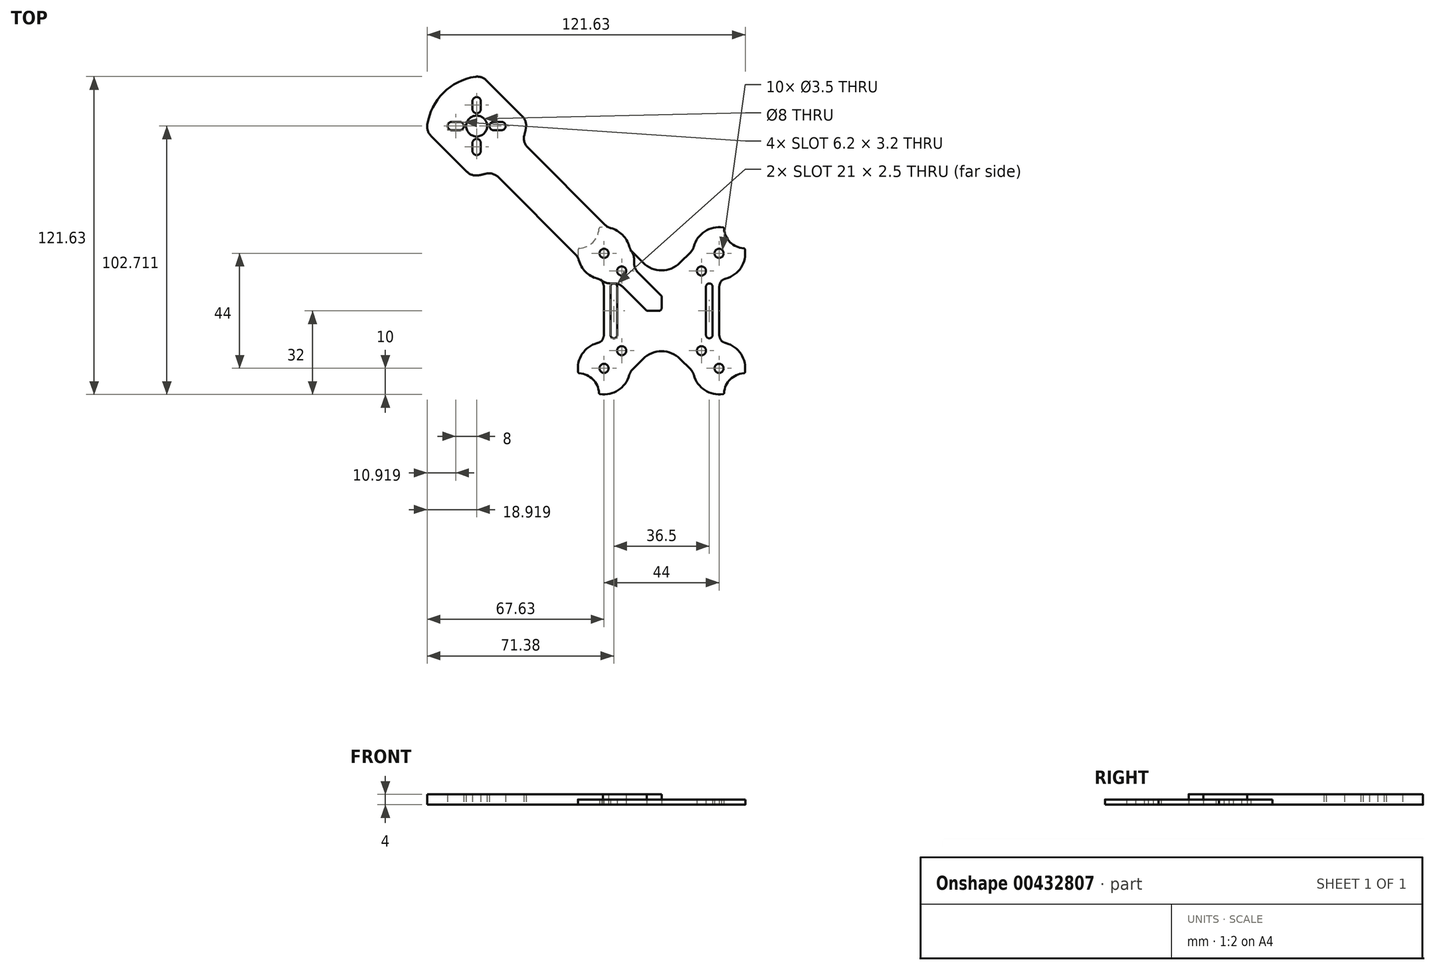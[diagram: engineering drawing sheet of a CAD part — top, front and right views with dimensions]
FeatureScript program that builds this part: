
annotation { "Feature Type Name" : "Feature", "Feature Type Description" : "" }
export const myFeature = defineFeature(function(context is Context, id is Id, definition is map)
    precondition{}
    {
        {
            var Q0;
            Q0=qCreatedBy(makeId("Top.planeOp"),FACE);
            var sketch = newSketch(context, id + "F0", { "sketchPlane" : qUnion([Q0])});
            skCircle(sketch, "E0", {"center": v(0, 0) * mm, "radius": 100 * mm, "construction": true});
            skLineSegment(sketch, "E1", {"start": v(0, 0) * mm, "end": v(-70.71, 70.71) * mm, "construction": true});
            skLineSegment(sketch, "E2", {"start": v(-53.4, 64.72) * mm, "end": v(-21.63, 32.95) * mm});
            skLineSegment(sketch, "E3", {"start": v(-64.72, 53.4) * mm, "end": v(-32.95, 21.63) * mm});
            skCircle(sketch, "E4", {"center": v(-70.71, 70.71) * mm, "radius": 4 * mm});
            skLineSegment(sketch, "E5", {"start": v(-70.71, 70.71) * mm, "end": v(-86.27, 86.27) * mm, "construction": true});
            skLineSegment(sketch, "E6", {"start": v(-70.71, 70.71) * mm, "end": v(-70.71, 77.21) * mm, "construction": true});
            skLineSegment(sketch, "E7", {"start": v(-70.71, 77.21) * mm, "end": v(-70.71, 80.21) * mm, "construction": true});
            skArc(sketch, "E8.0.startCap", {"start": v(-69.11, 77.21) * mm, "mid": v(-70.71, 75.61) * mm, "end": v(-72.31, 77.21) * mm});
            skArc(sketch, "E8.0.endCap", {"start": v(-72.31, 80.21) * mm, "mid": v(-70.71, 81.81) * mm, "end": v(-69.11, 80.21) * mm});
            skLineSegment(sketch, "E8.0.left", {"start": v(-72.31, 77.21) * mm, "end": v(-72.31, 80.21) * mm});
            skLineSegment(sketch, "E8.0.right", {"start": v(-69.11, 77.21) * mm, "end": v(-69.11, 80.21) * mm});
            skArc(sketch, "E9.1.0", {"start": v(-80.21, 69.11) * mm, "mid": v(-81.81, 70.71) * mm, "end": v(-80.21, 72.31) * mm});
            skLineSegment(sketch, "E9.1.1", {"start": v(-77.21, 69.11) * mm, "end": v(-80.21, 69.11) * mm});
            skArc(sketch, "E9.1.2", {"start": v(-77.21, 72.31) * mm, "mid": v(-75.61, 70.71) * mm, "end": v(-77.21, 69.11) * mm});
            skLineSegment(sketch, "E9.1.3", {"start": v(-77.21, 72.31) * mm, "end": v(-80.21, 72.31) * mm});
            skLineSegment(sketch, "E9.1.4", {"start": v(-77.21, 70.71) * mm, "end": v(-80.21, 70.71) * mm, "construction": true});
            skLineSegment(sketch, "E9.1.5", {"start": v(-70.71, 70.71) * mm, "end": v(-77.21, 70.71) * mm, "construction": true});
            skArc(sketch, "E9.2.0", {"start": v(-69.11, 61.21) * mm, "mid": v(-70.71, 59.61) * mm, "end": v(-72.31, 61.21) * mm});
            skLineSegment(sketch, "E9.2.1", {"start": v(-69.11, 64.21) * mm, "end": v(-69.11, 61.21) * mm});
            skArc(sketch, "E9.2.2", {"start": v(-72.31, 64.21) * mm, "mid": v(-70.71, 65.81) * mm, "end": v(-69.11, 64.21) * mm});
            skLineSegment(sketch, "E9.2.3", {"start": v(-72.31, 64.21) * mm, "end": v(-72.31, 61.21) * mm});
            skLineSegment(sketch, "E9.2.4", {"start": v(-70.71, 64.21) * mm, "end": v(-70.71, 61.21) * mm, "construction": true});
            skLineSegment(sketch, "E9.2.5", {"start": v(-70.71, 70.71) * mm, "end": v(-70.71, 64.21) * mm, "construction": true});
            skArc(sketch, "E9.3.0", {"start": v(-61.21, 72.31) * mm, "mid": v(-59.61, 70.71) * mm, "end": v(-61.21, 69.11) * mm});
            skLineSegment(sketch, "E9.3.1", {"start": v(-64.21, 72.31) * mm, "end": v(-61.21, 72.31) * mm});
            skArc(sketch, "E9.3.2", {"start": v(-64.21, 69.11) * mm, "mid": v(-65.81, 70.71) * mm, "end": v(-64.21, 72.31) * mm});
            skLineSegment(sketch, "E9.3.3", {"start": v(-64.21, 69.11) * mm, "end": v(-61.21, 69.11) * mm});
            skLineSegment(sketch, "E9.3.4", {"start": v(-64.21, 70.71) * mm, "end": v(-61.21, 70.71) * mm, "construction": true});
            skLineSegment(sketch, "E9.3.5", {"start": v(-70.71, 70.71) * mm, "end": v(-64.21, 70.71) * mm, "construction": true});
            skCircle(sketch, "E10", {"center": v(-15.25, 15.25) * mm, "radius": 1.75 * mm});
            skCircle(sketch, "E11", {"center": v(-70.71, 70.71) * mm, "radius": 64.25 * mm, "construction": true});
            skLineSegment(sketch, "E12.bottom", {"start": v(-72.83, 51.62) * mm, "end": v(-89.8, 68.59) * mm});
            skLineSegment(sketch, "E12.top", {"start": v(-51.62, 72.83) * mm, "end": v(-68.59, 89.8) * mm});
            skLineSegment(sketch, "E12.left", {"start": v(-68.59, 47.38) * mm, "end": v(-47.38, 68.59) * mm, "construction": true});
            skLineSegment(sketch, "E12.right", {"start": v(-94.05, 72.83) * mm, "end": v(-72.83, 94.05) * mm, "construction": true});
            skArc(sketch, "E13", {"start": v(-68.59, 89.8) * mm, "mid": v(-83.44, 83.44) * mm, "end": v(-89.8, 68.59) * mm});
            skArc(sketch, "E14", {"start": v(-72.83, 51.62) * mm, "mid": v(-68.69, 52.12) * mm, "end": v(-64.72, 53.4) * mm});
            skArc(sketch, "E15.trimOffspring", {"start": v(-53.4, 64.72) * mm, "mid": v(-52.12, 68.69) * mm, "end": v(-51.62, 72.83) * mm});
            skCircle(sketch, "E16", {"center": v(-22, 22) * mm, "radius": 1.75 * mm});
            skLineSegment(sketch, "E17", {"start": v(-14.7, 9.04) * mm, "end": v(-5.66, 0) * mm});
            skLineSegment(sketch, "E18", {"start": v(-9.04, 14.7) * mm, "end": v(0, 5.66) * mm});
            skLineSegment(sketch, "E19", {"start": v(0, 5.66) * mm, "end": v(0, 0) * mm});
            skLineSegment(sketch, "E20", {"start": v(-5.66, 0) * mm, "end": v(0, 0) * mm});
            skArc(sketch, "E21", {"start": v(-31.66, 19.4) * mm, "mid": v(-29.07, 14.93) * mm, "end": v(-24.6, 12.34) * mm});
            skLineSegment(sketch, "E22.trimOffspring", {"start": v(-23.28, 11.96) * mm, "end": v(-22.37, 11.05) * mm});
            skLineSegment(sketch, "E23.trimOffspring", {"start": v(-11.96, 23.28) * mm, "end": v(-11.05, 22.37) * mm});
            skArc(sketch, "E24.trimOffspring", {"start": v(-12.34, 24.6) * mm, "mid": v(-14.93, 29.07) * mm, "end": v(-19.4, 31.66) * mm});
            skPoint(sketch, "E25.visualSharp", {"position": v(-31.9, 20.59) * mm});
            skArc(sketch, "E25.filletArc", {"start": v(-31.66, 19.4) * mm, "mid": v(-32.16, 20.6) * mm, "end": v(-32.95, 21.63) * mm});
            skPoint(sketch, "E26.visualSharp", {"position": v(-23.41, 12.1) * mm});
            skArc(sketch, "E26.filletArc", {"start": v(-22.37, 11.05) * mm, "mid": v(-23.4, 11.84) * mm, "end": v(-24.6, 12.34) * mm});
            skPoint(sketch, "E27.visualSharp", {"position": v(-12.1, 23.41) * mm});
            skArc(sketch, "E27.filletArc", {"start": v(-12.34, 24.6) * mm, "mid": v(-11.84, 23.4) * mm, "end": v(-11.05, 22.37) * mm});
            skPoint(sketch, "E28.visualSharp", {"position": v(-20.59, 31.9) * mm});
            skArc(sketch, "E28.filletArc", {"start": v(-21.63, 32.95) * mm, "mid": v(-20.6, 32.16) * mm, "end": v(-19.4, 31.66) * mm});
            skLineSegment(sketch, "E29", {"start": v(-19.74, 10.5) * mm, "end": v(-18.23, 10.5) * mm});
            skLineSegment(sketch, "E30", {"start": v(-10.5, 19.74) * mm, "end": v(-10.5, 18.23) * mm});
            skPoint(sketch, "E31.visualSharp", {"position": v(-16.16, 10.5) * mm});
            skArc(sketch, "E31.filletArc", {"start": v(-14.7, 9.04) * mm, "mid": v(-16.31, 10.12) * mm, "end": v(-18.23, 10.5) * mm});
            skPoint(sketch, "E32.visualSharp", {"position": v(-10.5, 16.16) * mm});
            skArc(sketch, "E32.filletArc", {"start": v(-10.5, 18.23) * mm, "mid": v(-10.12, 16.31) * mm, "end": v(-9.04, 14.7) * mm});
            skPoint(sketch, "E33.visualSharp", {"position": v(-10.5, 21.81) * mm});
            skArc(sketch, "E33.filletArc", {"start": v(-10.5, 19.74) * mm, "mid": v(-10.88, 21.66) * mm, "end": v(-11.96, 23.28) * mm});
            skPoint(sketch, "E34.visualSharp", {"position": v(-21.81, 10.5) * mm});
            skArc(sketch, "E34.filletArc", {"start": v(-23.28, 11.96) * mm, "mid": v(-21.66, 10.88) * mm, "end": v(-19.74, 10.5) * mm});
            skSolve(sketch);
        }
        {
            var Q0;
            Q0=makeQuery(id+"F0.imprint","IMPRINT",FACE,{"disambiguationData":[TD([[makeQuery(id+"F0.imprint","IMPRINT",EDGE,{"derivedFrom":sQuery(id+"F0.wireOp",EDGE,"E2")}),-1.0]])]});
            extrude(context, id + "F1", {"entities" : qUnion([Q0]), "depth" : 4 * mm});
        }
        {
            var Q0;
            Q0=makeQuery(id+"F1.opExtrude","SWEPT_EDGE",EDGE,{"disambiguationData":[OSD([sQuery(id+"F0.wireOp",EDGE,"E3"),sQuery(id+"F0.wireOp",EDGE,"Om9wZ7ED-7TQL-2rBA-pihk-640UzqtQJKO6")])]});
            var Q1;
            Q1=makeQuery(id+"F1.opExtrude","SWEPT_EDGE",EDGE,{"disambiguationData":[OSD([sQuery(id+"F0.wireOp",EDGE,"E3"),sQuery(id+"F0.wireOp",EDGE,"E14")])]});
            var Q2;
            Q2=makeQuery(id+"F1.opExtrude","SWEPT_EDGE",EDGE,{"disambiguationData":[OSD([sQuery(id+"F0.wireOp",EDGE,"E2"),sQuery(id+"F0.wireOp",EDGE,"E15.trimOffspring")])]});
            var Q3;
            Q3=makeQuery(id+"F1.opExtrude","SWEPT_EDGE",EDGE,{"disambiguationData":[OSD([sQuery(id+"F0.wireOp",EDGE,"E12.bottom"),sQuery(id+"F0.wireOp",EDGE,"E14")])]});
            var Q4;
            Q4=makeQuery(id+"F1.opExtrude","SWEPT_EDGE",EDGE,{"disambiguationData":[OSD([sQuery(id+"F0.wireOp",EDGE,"E12.top"),sQuery(id+"F0.wireOp",EDGE,"E15.trimOffspring")])]});
            var Q5;
            Q5=makeQuery(id+"F1.opExtrude","SWEPT_EDGE",EDGE,{"disambiguationData":[OSD([sQuery(id+"F0.wireOp",EDGE,"E12.bottom"),sQuery(id+"F0.wireOp",EDGE,"E13")])]});
            var Q6;
            Q6=makeQuery(id+"F1.opExtrude","SWEPT_EDGE",EDGE,{"disambiguationData":[OSD([sQuery(id+"F0.wireOp",EDGE,"E12.top"),sQuery(id+"F0.wireOp",EDGE,"E13")])]});
            fillet(context, id + "F2", {"entities" : qUnion([Q0, Q1, Q2, Q3, Q4, Q5, Q6]), "radius" : 5 * mm, "tangentPropagation" : true, "allowEdgeOverflow" : false});
        }
        {
            var Q0;
            Q0=makeQuery(id+"F1.opExtrude","SWEPT_EDGE",EDGE,{"disambiguationData":[OSD([sQuery(id+"F0.wireOp",EDGE,"E19"),sQuery(id+"F0.wireOp",EDGE,"E20")])]});
            fillet(context, id + "F3", {"entities" : qUnion([Q0]), "radius" : 1 * mm, "tangentPropagation" : true, "allowEdgeOverflow" : false});
        }
        {
            var Q0;
            Q0=qCreatedBy(makeId("Top.planeOp"),FACE);
            var sketch = newSketch(context, id + "F4", { "sketchPlane" : qUnion([Q0])});
            skArc(sketch, "E35", {"start": v(-12.34, 24.6) * mm, "mid": v(-16.53, 30.37) * mm, "end": v(-23.49, 31.89) * mm});
            skLineSegment(sketch, "E36.bottom", {"start": v(-18.25, 10.5) * mm, "end": v(-18.25, 10.5) * mm});
            skLineSegment(sketch, "E36.left", {"start": v(-19.5, 9.25) * mm, "end": v(-19.5, 0) * mm});
            skLineSegment(sketch, "E36.right", {"start": v(-17, 9.25) * mm, "end": v(-17, 0) * mm});
            skPoint(sketch, "E37.visualSharp", {"position": v(-17, 10.5) * mm});
            skArc(sketch, "E37.filletArc", {"start": v(-17, 9.25) * mm, "mid": v(-17.37, 10.13) * mm, "end": v(-18.25, 10.5) * mm});
            skPoint(sketch, "E38.visualSharp", {"position": v(-19.5, 10.5) * mm});
            skArc(sketch, "E38.filletArc", {"start": v(-18.25, 10.5) * mm, "mid": v(-19.13, 10.13) * mm, "end": v(-19.5, 9.25) * mm});
            skLineSegment(sketch, "E39", {"start": v(-23.46, 12.15) * mm, "end": v(-22.37, 11.05) * mm});
            skLineSegment(sketch, "E40", {"start": v(-11.05, 22.37) * mm, "end": v(-7.07, 18.38) * mm});
            skLineSegment(sketch, "E41", {"start": v(-22, 22) * mm, "end": v(0, 0) * mm, "construction": true});
            skLineSegment(sketch, "E42", {"start": v(-22, 8.62) * mm, "end": v(-22, 0) * mm});
            skPoint(sketch, "E43.visualSharp", {"position": v(-22, 10.69) * mm});
            skArc(sketch, "E43.filletArc", {"start": v(-22, 8.62) * mm, "mid": v(-22.38, 10.53) * mm, "end": v(-23.46, 12.15) * mm});
            skPoint(sketch, "E44.visualSharp", {"position": v(-23.41, 12.1) * mm});
            skArc(sketch, "E44.filletArc", {"start": v(-22.37, 11.05) * mm, "mid": v(-23.4, 11.84) * mm, "end": v(-24.6, 12.34) * mm});
            skPoint(sketch, "E45.visualSharp", {"position": v(-12.1, 23.41) * mm});
            skArc(sketch, "E45.filletArc", {"start": v(-12.34, 24.6) * mm, "mid": v(-11.84, 23.4) * mm, "end": v(-11.05, 22.37) * mm});
            skLineSegment(sketch, "E46", {"start": v(-22, 22) * mm, "end": v(-29.07, 29.07) * mm, "construction": true});
            skArc(sketch, "E47", {"start": v(-31.42, 23.91) * mm, "mid": v(-26.24, 26.24) * mm, "end": v(-23.91, 31.42) * mm});
            skLineSegment(sketch, "E48", {"start": v(-29.07, 29.07) * mm, "end": v(-31.9, 31.9) * mm, "construction": true});
            skArc(sketch, "E49.trimOffspring", {"start": v(-31.89, 23.49) * mm, "mid": v(-30.37, 16.53) * mm, "end": v(-24.6, 12.34) * mm});
            skPoint(sketch, "E50.visualSharp", {"position": v(-23.9, 31.82) * mm});
            skArc(sketch, "E50.filletArc", {"start": v(-23.49, 31.89) * mm, "mid": v(-23.78, 31.73) * mm, "end": v(-23.91, 31.42) * mm});
            skPoint(sketch, "E51.visualSharp", {"position": v(-31.82, 23.9) * mm});
            skArc(sketch, "E51.filletArc", {"start": v(-31.42, 23.91) * mm, "mid": v(-31.73, 23.78) * mm, "end": v(-31.89, 23.49) * mm});
            skCircle(sketch, "E52", {"center": v(-22, 22) * mm, "radius": 1.75 * mm});
            skCircle(sketch, "E53", {"center": v(-15.25, 15.25) * mm, "radius": 1.75 * mm});
            skArc(sketch, "E54.MirrorCS", {"start": v(23.49, 31.89) * mm, "mid": v(23.78, 31.73) * mm, "end": v(23.91, 31.42) * mm});
            skArc(sketch, "E55.MirrorCS", {"start": v(31.42, 23.91) * mm, "mid": v(31.73, 23.78) * mm, "end": v(31.89, 23.49) * mm});
            skArc(sketch, "E56.MirrorCS", {"start": v(18.25, 10.5) * mm, "mid": v(19.13, 10.13) * mm, "end": v(19.5, 9.25) * mm});
            skLineSegment(sketch, "E57.MirrorCS", {"start": v(23.46, 12.15) * mm, "end": v(22.37, 11.05) * mm});
            skArc(sketch, "E58.MirrorCS", {"start": v(12.34, 24.6) * mm, "mid": v(11.84, 23.4) * mm, "end": v(11.05, 22.37) * mm});
            skArc(sketch, "E59.MirrorCS", {"start": v(22, 8.62) * mm, "mid": v(22.38, 10.53) * mm, "end": v(23.46, 12.15) * mm});
            skArc(sketch, "E60.MirrorCS", {"start": v(17, 9.25) * mm, "mid": v(17.37, 10.13) * mm, "end": v(18.25, 10.5) * mm});
            skArc(sketch, "E61.MirrorCS", {"start": v(22.37, 11.05) * mm, "mid": v(23.4, 11.84) * mm, "end": v(24.6, 12.34) * mm});
            skPoint(sketch, "E62.MirrorP", {"position": v(23.9, 31.82) * mm});
            skArc(sketch, "E63.MirrorCS", {"start": v(31.42, 23.91) * mm, "mid": v(26.24, 26.24) * mm, "end": v(23.91, 31.42) * mm});
            skPoint(sketch, "E64.MirrorP", {"position": v(31.82, 23.9) * mm});
            skPoint(sketch, "E65.MirrorP", {"position": v(17, 10.5) * mm});
            skCircle(sketch, "E66.MirrorC", {"center": v(22, 22) * mm, "radius": 1.75 * mm});
            skLineSegment(sketch, "E67.MirrorCS", {"start": v(29.07, 29.07) * mm, "end": v(31.9, 31.9) * mm, "construction": true});
            skLineSegment(sketch, "E68.MirrorCS", {"start": v(17, 9.25) * mm, "end": v(17, 0) * mm});
            skLineSegment(sketch, "E69.MirrorCS", {"start": v(18.25, 10.5) * mm, "end": v(18.25, 10.5) * mm});
            skPoint(sketch, "E70.MirrorP", {"position": v(19.5, 10.5) * mm});
            skArc(sketch, "E71.MirrorCS", {"start": v(12.34, 24.6) * mm, "mid": v(16.53, 30.37) * mm, "end": v(23.49, 31.89) * mm});
            skArc(sketch, "E72.MirrorCS", {"start": v(31.89, 23.49) * mm, "mid": v(30.37, 16.53) * mm, "end": v(24.6, 12.34) * mm});
            skLineSegment(sketch, "E73.MirrorCS", {"start": v(19.5, 9.25) * mm, "end": v(19.5, 0) * mm});
            skLineSegment(sketch, "E74.MirrorCS", {"start": v(22, 22) * mm, "end": v(29.07, 29.07) * mm, "construction": true});
            skPoint(sketch, "E75.MirrorP", {"position": v(12.1, 23.41) * mm});
            skPoint(sketch, "E76.MirrorP", {"position": v(23.41, 12.1) * mm});
            skPoint(sketch, "E77.MirrorP", {"position": v(22, 10.69) * mm});
            skLineSegment(sketch, "E78.MirrorCS", {"start": v(11.05, 22.37) * mm, "end": v(7.07, 18.38) * mm});
            skLineSegment(sketch, "E79.MirrorCS", {"start": v(22, 22) * mm, "end": v(0, 0) * mm, "construction": true});
            skCircle(sketch, "E80.MirrorC", {"center": v(15.25, 15.25) * mm, "radius": 1.75 * mm});
            skLineSegment(sketch, "E81.MirrorCS", {"start": v(22, 8.62) * mm, "end": v(22, 0) * mm});
            skArc(sketch, "E82.MirrorCS", {"start": v(23.49, -31.89) * mm, "mid": v(23.78, -31.73) * mm, "end": v(23.91, -31.42) * mm});
            skArc(sketch, "E83.MirrorCS", {"start": v(-23.49, -31.89) * mm, "mid": v(-23.78, -31.73) * mm, "end": v(-23.91, -31.42) * mm});
            skArc(sketch, "E84.MirrorCS", {"start": v(-31.42, -23.91) * mm, "mid": v(-31.73, -23.78) * mm, "end": v(-31.89, -23.49) * mm});
            skArc(sketch, "E85.MirrorCS", {"start": v(31.42, -23.91) * mm, "mid": v(31.73, -23.78) * mm, "end": v(31.89, -23.49) * mm});
            skArc(sketch, "E86.MirrorCS", {"start": v(-17, -9.25) * mm, "mid": v(-17.37, -10.13) * mm, "end": v(-18.25, -10.5) * mm});
            skArc(sketch, "E87.MirrorCS", {"start": v(-18.25, -10.5) * mm, "mid": v(-19.13, -10.13) * mm, "end": v(-19.5, -9.25) * mm});
            skArc(sketch, "E88.MirrorCS", {"start": v(18.25, -10.5) * mm, "mid": v(19.13, -10.13) * mm, "end": v(19.5, -9.25) * mm});
            skLineSegment(sketch, "E89.MirrorCS", {"start": v(23.46, -12.15) * mm, "end": v(22.37, -11.05) * mm});
            skArc(sketch, "E90.MirrorCS", {"start": v(22.37, -11.05) * mm, "mid": v(23.4, -11.84) * mm, "end": v(24.6, -12.34) * mm});
            skArc(sketch, "E91.MirrorCS", {"start": v(-12.34, -24.6) * mm, "mid": v(-11.84, -23.4) * mm, "end": v(-11.05, -22.37) * mm});
            skArc(sketch, "E92.MirrorCS", {"start": v(-22.37, -11.05) * mm, "mid": v(-23.4, -11.84) * mm, "end": v(-24.6, -12.34) * mm});
            skArc(sketch, "E93.MirrorCS", {"start": v(12.34, -24.6) * mm, "mid": v(11.84, -23.4) * mm, "end": v(11.05, -22.37) * mm});
            skArc(sketch, "E94.MirrorCS", {"start": v(17, -9.25) * mm, "mid": v(17.37, -10.13) * mm, "end": v(18.25, -10.5) * mm});
            skLineSegment(sketch, "E95.MirrorCS", {"start": v(-23.46, -12.15) * mm, "end": v(-22.37, -11.05) * mm});
            skArc(sketch, "E96.MirrorCS", {"start": v(-22, -8.62) * mm, "mid": v(-22.38, -10.53) * mm, "end": v(-23.46, -12.15) * mm});
            skArc(sketch, "E97.MirrorCS", {"start": v(22, -8.62) * mm, "mid": v(22.38, -10.53) * mm, "end": v(23.46, -12.15) * mm});
            skPoint(sketch, "E98.MirrorP", {"position": v(-23.9, -31.82) * mm});
            skPoint(sketch, "E99.MirrorP", {"position": v(17, -10.5) * mm});
            skLineSegment(sketch, "E100.MirrorCS", {"start": v(-18.25, -10.5) * mm, "end": v(-18.25, -10.5) * mm});
            skPoint(sketch, "E101.MirrorP", {"position": v(23.41, -12.1) * mm});
            skCircle(sketch, "E102.MirrorC", {"center": v(22, -22) * mm, "radius": 1.75 * mm});
            skLineSegment(sketch, "E103.MirrorCS", {"start": v(11.05, -22.37) * mm, "end": v(7.07, -18.38) * mm});
            skPoint(sketch, "E104.MirrorP", {"position": v(-19.5, -10.5) * mm});
            skLineSegment(sketch, "E105.MirrorCS", {"start": v(22, -8.62) * mm, "end": v(22, 0) * mm});
            skPoint(sketch, "E106.MirrorP", {"position": v(19.5, -10.5) * mm});
            skArc(sketch, "E107.MirrorCS", {"start": v(12.34, -24.6) * mm, "mid": v(16.53, -30.37) * mm, "end": v(23.49, -31.89) * mm});
            skPoint(sketch, "E108.MirrorP", {"position": v(-31.82, -23.9) * mm});
            skLineSegment(sketch, "E109.MirrorCS", {"start": v(-22, -22) * mm, "end": v(-29.07, -29.07) * mm, "construction": true});
            skPoint(sketch, "E110.MirrorP", {"position": v(-22, -10.69) * mm});
            skPoint(sketch, "E111.MirrorP", {"position": v(31.82, -23.9) * mm});
            skLineSegment(sketch, "E112.MirrorCS", {"start": v(-22, -8.62) * mm, "end": v(-22, 0) * mm});
            skLineSegment(sketch, "E113.MirrorCS", {"start": v(-22, -22) * mm, "end": v(0, 0) * mm, "construction": true});
            skPoint(sketch, "E114.MirrorP", {"position": v(12.1, -23.41) * mm});
            skLineSegment(sketch, "E115.MirrorCS", {"start": v(-11.05, -22.37) * mm, "end": v(-7.07, -18.38) * mm});
            skCircle(sketch, "E116.MirrorC", {"center": v(-15.25, -15.25) * mm, "radius": 1.75 * mm});
            skLineSegment(sketch, "E117.MirrorCS", {"start": v(22, -22) * mm, "end": v(29.07, -29.07) * mm, "construction": true});
            skArc(sketch, "E118.MirrorCS", {"start": v(31.42, -23.91) * mm, "mid": v(26.24, -26.24) * mm, "end": v(23.91, -31.42) * mm});
            skArc(sketch, "E119.MirrorCS", {"start": v(-31.42, -23.91) * mm, "mid": v(-26.24, -26.24) * mm, "end": v(-23.91, -31.42) * mm});
            skPoint(sketch, "E120.MirrorP", {"position": v(-12.1, -23.41) * mm});
            skLineSegment(sketch, "E121.MirrorCS", {"start": v(-29.07, -29.07) * mm, "end": v(-31.9, -31.9) * mm, "construction": true});
            skArc(sketch, "E122.MirrorCS", {"start": v(31.89, -23.49) * mm, "mid": v(30.37, -16.53) * mm, "end": v(24.6, -12.34) * mm});
            skLineSegment(sketch, "E123.MirrorCS", {"start": v(19.5, -9.25) * mm, "end": v(19.5, 0) * mm});
            skLineSegment(sketch, "E124.MirrorCS", {"start": v(-17, -9.25) * mm, "end": v(-17, 0) * mm});
            skArc(sketch, "E125.MirrorCS", {"start": v(-31.89, -23.49) * mm, "mid": v(-30.37, -16.53) * mm, "end": v(-24.6, -12.34) * mm});
            skCircle(sketch, "E126.MirrorC", {"center": v(-22, -22) * mm, "radius": 1.75 * mm});
            skPoint(sketch, "E127.MirrorP", {"position": v(-17, -10.5) * mm});
            skLineSegment(sketch, "E128.MirrorCS", {"start": v(17, -9.25) * mm, "end": v(17, 0) * mm});
            skLineSegment(sketch, "E129.MirrorCS", {"start": v(22, -22) * mm, "end": v(0, 0) * mm, "construction": true});
            skPoint(sketch, "E130.MirrorP", {"position": v(22, -10.69) * mm});
            skLineSegment(sketch, "E131.MirrorCS", {"start": v(18.25, -10.5) * mm, "end": v(18.25, -10.5) * mm});
            skArc(sketch, "E132.MirrorCS", {"start": v(-12.34, -24.6) * mm, "mid": v(-16.53, -30.37) * mm, "end": v(-23.49, -31.89) * mm});
            skLineSegment(sketch, "E133.MirrorCS", {"start": v(29.07, -29.07) * mm, "end": v(31.9, -31.9) * mm, "construction": true});
            skPoint(sketch, "E134.MirrorP", {"position": v(23.9, -31.82) * mm});
            skLineSegment(sketch, "E135.MirrorCS", {"start": v(-19.5, -9.25) * mm, "end": v(-19.5, 0) * mm});
            skCircle(sketch, "E136.MirrorC", {"center": v(15.25, -15.25) * mm, "radius": 1.75 * mm});
            skPoint(sketch, "E137.MirrorP", {"position": v(-23.41, -12.1) * mm});
            skPoint(sketch, "E138.visualSharp", {"position": v(0, 11.31) * mm});
            skArc(sketch, "E138.filletArc", {"start": v(-7.07, 18.38) * mm, "mid": v(0, 15.46) * mm, "end": v(7.07, 18.38) * mm});
            skPoint(sketch, "E139.visualSharp", {"position": v(0, -11.31) * mm});
            skArc(sketch, "E139.filletArc", {"start": v(7.07, -18.38) * mm, "mid": v(0, -15.46) * mm, "end": v(-7.07, -18.38) * mm});
            skSolve(sketch);
        }
        {
            var Q0;
            Q0 = qSketchRegion(id + "F4", true);
            extrude(context, id + "F5", {"entities" : qUnion([Q0]), "depth" : 2 * mm});
        }
    });
